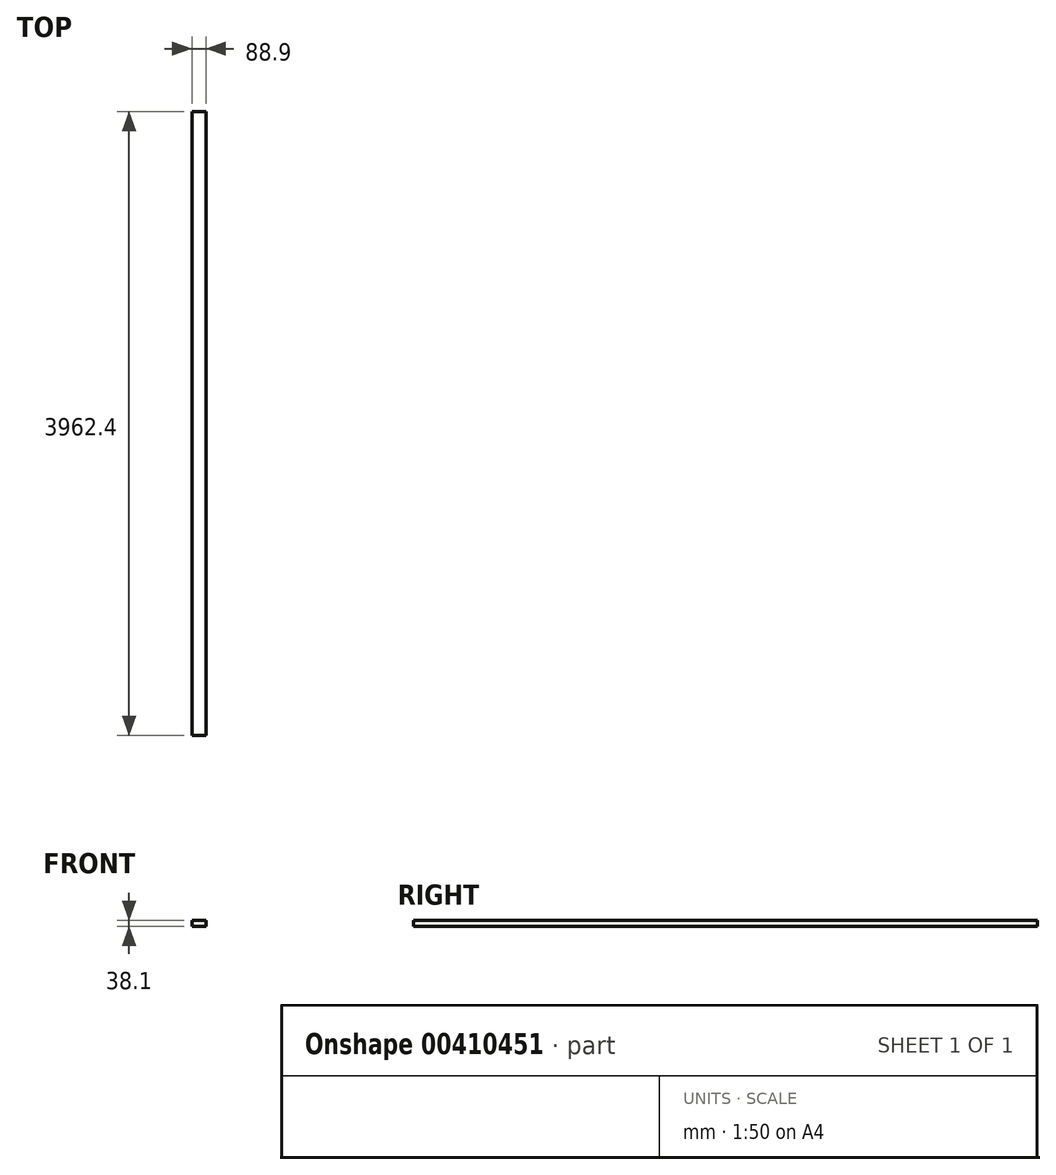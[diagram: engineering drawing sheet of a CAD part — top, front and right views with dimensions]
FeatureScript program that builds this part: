
annotation { "Feature Type Name" : "Feature", "Feature Type Description" : "" }
export const myFeature = defineFeature(function(context is Context, id is Id, definition is map)
    precondition{}
    {
        {
            var Q0;
            Q0=qCreatedBy(makeId("Right.planeOp"),FACE);
            var sketch = newSketch(context, id + "F0", { "sketchPlane" : qUnion([Q0])});
            skLineSegment(sketch, "E0.bottom", {"start": v(-1981.2, 19.05) * mm, "end": v(1981.2, 19.05) * mm});
            skLineSegment(sketch, "E0.top", {"start": v(-1981.2, -19.05) * mm, "end": v(1981.2, -19.05) * mm});
            skLineSegment(sketch, "E0.left", {"start": v(-1981.2, 19.05) * mm, "end": v(-1981.2, -19.05) * mm});
            skLineSegment(sketch, "E0.right", {"start": v(1981.2, 19.05) * mm, "end": v(1981.2, -19.05) * mm});
            skPoint(sketch, "E0.middle", {"position": v(0, 0) * mm});
            skSolve(sketch);
        }
        {
            var Q0;
            Q0=qSketchRegion(id+"F0",true);
            extrude(context, id + "F1", {"entities" : qUnion([Q0]), "depth" : 88.9 * mm, "offsetDistance" : 25.4 * mm, "symmetric" : true});
        }
    });
